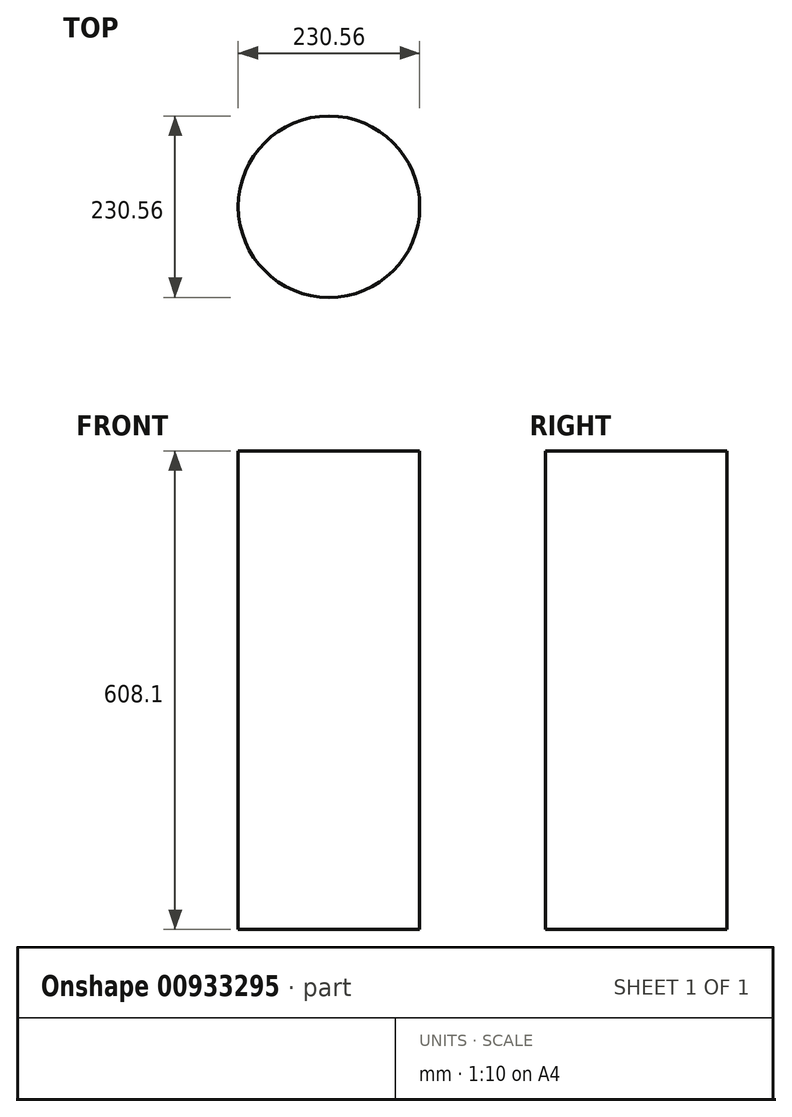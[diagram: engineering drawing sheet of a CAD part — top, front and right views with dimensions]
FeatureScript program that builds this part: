
annotation { "Feature Type Name" : "Feature", "Feature Type Description" : "" }
export const myFeature = defineFeature(function(context is Context, id is Id, definition is map)
    precondition{}
    {
        {
            var Q0;
            Q0=qCreatedBy(makeId("Top.planeOp"),FACE);
            var sketch = newSketch(context, id + "F0", { "sketchPlane" : qUnion([Q0])});
            skCircle(sketch, "E0", {"center": v(0, 0) * mm, "radius": 115.28 * mm});
            skSolve(sketch);
        }
        {
            var Q0;
            Q0 = qSketchRegion(id + "F0", true);
            extrude(context, id + "F1", {"entities" : qUnion([Q0]), "oppositeDirection" : true, "depth" : 608.1 * mm, "offsetDistance" : 25.4 * mm});
        }
    });
